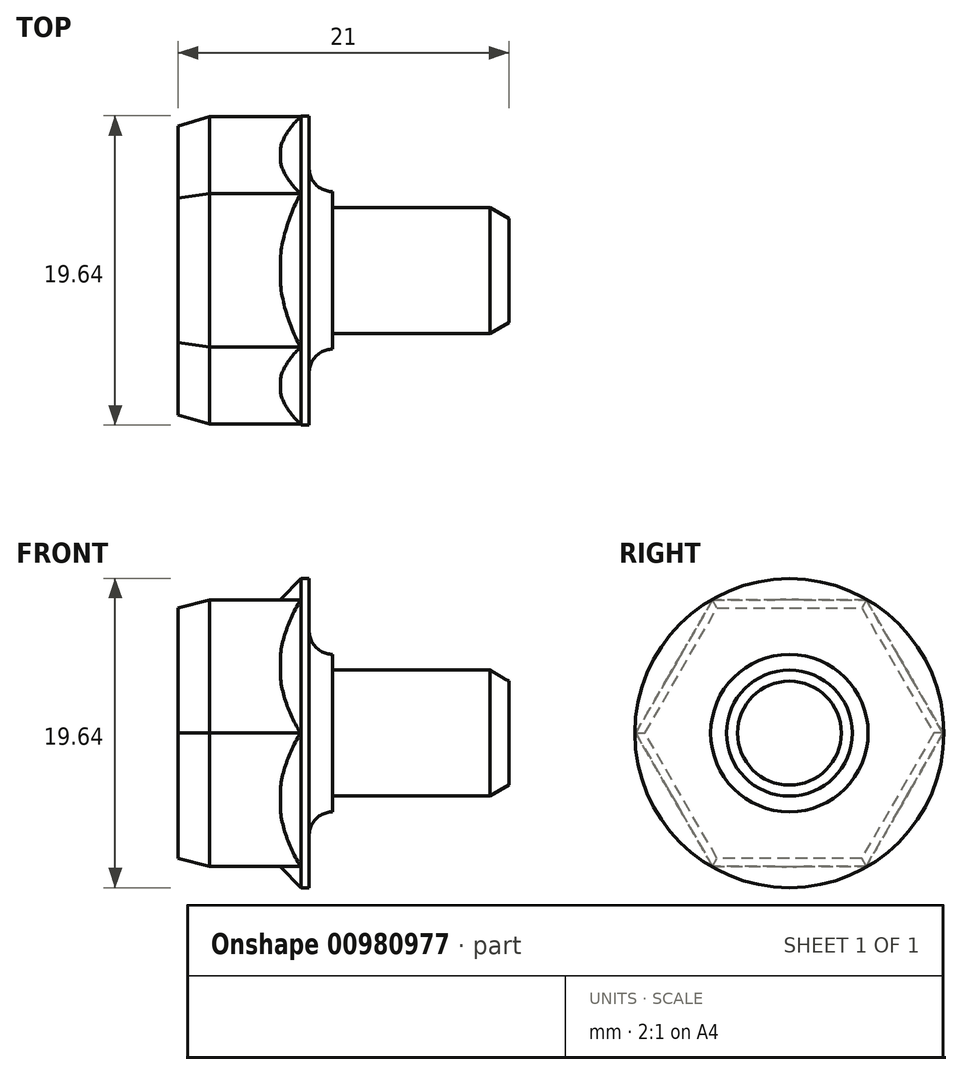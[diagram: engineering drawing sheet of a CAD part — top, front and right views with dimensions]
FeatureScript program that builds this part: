
annotation { "Feature Type Name" : "Feature", "Feature Type Description" : "" }
export const myFeature = defineFeature(function(context is Context, id is Id, definition is map)
    precondition{}
    {
        {
            var Q0;
            Q0=qCreatedBy(makeId("Right.planeOp"),FACE);
            var sketch = newSketch(context, id + "F0", { "sketchPlane" : qUnion([Q0])});
            skCircle(sketch, "E0.cCircle", {"center": v(0, 0) * mm, "radius": 8.45 * mm, "construction": true});
            skLineSegment(sketch, "E0.0", {"start": v(-4.88, 8.45) * mm, "end": v(4.88, 8.45) * mm});
            skLineSegment(sketch, "E0.1", {"start": v(4.88, 8.45) * mm, "end": v(9.76, 0) * mm});
            skLineSegment(sketch, "E0.2", {"start": v(9.76, 0) * mm, "end": v(4.88, -8.45) * mm});
            skLineSegment(sketch, "E0.3", {"start": v(4.88, -8.45) * mm, "end": v(-4.88, -8.45) * mm});
            skLineSegment(sketch, "E0.4", {"start": v(-4.88, -8.45) * mm, "end": v(-9.76, 0) * mm});
            skLineSegment(sketch, "E0.5", {"start": v(-9.76, 0) * mm, "end": v(-4.88, 8.45) * mm});
            skPoint(sketch, "E0.0.midPoint", {"position": v(0, 8.45) * mm});
            skSolve(sketch);
        }
        {
            var Q0;
            Q0=makeQuery(id+"F0.imprint","IMPRINT",FACE,{"disambiguationData":[TD([[makeQuery(id+"F0.imprint","IMPRINT",EDGE,{"derivedFrom":sQuery(id+"F0.wireOp",EDGE,"E0.0")}),-1.0]])]});
            extrude(context, id + "F1", {"entities" : qUnion([Q0]), "depth" : 8 * mm, "offsetDistance" : 25 * mm});
        }
        {
            var Q0;
            Q0=qCreatedBy(makeId("Front.planeOp"),FACE);
            var sketch = newSketch(context, id + "F2", { "sketchPlane" : qUnion([Q0])});
            skLineSegment(sketch, "E1", {"start": v(-6.63, 0) * mm, "end": v(40.7, 0) * mm, "construction": true});
            skLineSegment(sketch, "E2.bottom", {"start": v(6.5, 0) * mm, "end": v(8.31, 0) * mm});
            skLineSegment(sketch, "E2.top", {"start": v(6.5, 9.81) * mm, "end": v(8.31, 9.81) * mm});
            skLineSegment(sketch, "E2.left", {"start": v(6.5, 0) * mm, "end": v(6.5, 9.81) * mm});
            skLineSegment(sketch, "E2.right", {"start": v(8.32, 0) * mm, "end": v(8.31, 9.81) * mm});
            skLineSegment(sketch, "E3.top", {"start": v(9.81, 4) * mm, "end": v(21, 4) * mm});
            skLineSegment(sketch, "E3.right", {"start": v(21, 0) * mm, "end": v(21, 4) * mm});
            skLineSegment(sketch, "E4", {"start": v(7.81, 9.81) * mm, "end": v(6.5, 8.5) * mm});
            skArc(sketch, "E5", {"start": v(8.31, 6.5) * mm, "mid": v(8.75, 5.44) * mm, "end": v(9.81, 5) * mm});
            skLineSegment(sketch, "E6", {"start": v(9.81, 5) * mm, "end": v(18.14, 5) * mm, "construction": true});
            skLineSegment(sketch, "E7", {"start": v(9.81, 5) * mm, "end": v(9.81, 4) * mm});
            skLineSegment(sketch, "E8", {"start": v(8.31, 0) * mm, "end": v(21, 0) * mm});
            skSolve(sketch);
        }
        {
            var Q0;
            Q0=makeQuery(id+"F2.imprint","IMPRINT",FACE,{"disambiguationData":[TD([[makeQuery(id+"F2.imprint","IMPRINT",EDGE,{"derivedFrom":sQuery(id+"F2.wireOp",EDGE,"E2.right")}),-1.0]])]});
            var Q1;
            Q1=makeQuery(id+"F2.imprint","IMPRINT",FACE,{"disambiguationData":[TD([[makeQuery(id+"F2.imprint","IMPRINT",EDGE,{"derivedFrom":sQuery(id+"F2.wireOp",EDGE,"E3.bottom")}),1.0]])]});
            var Q2;
            Q2=makeQuery(id+"F2.imprint","IMPRINT",FACE,{"disambiguationData":[TD([[makeQuery(id+"F2.imprint","IMPRINT",EDGE,{"derivedFrom":sQuery(id+"F2.wireOp",EDGE,"E2.bottom")}),1.0]])]});
            var Q3;
            Q3=sQuery(id+"F2.wireOp",EDGE,"E1");
            revolve(context, id + "F3", {"operationType" : NewBodyOperationType.ADD, "surfaceOperationType" : NewSurfaceOperationType.NEW, "entities" : qUnion([Q0, Q1, Q2]), "axis" : qUnion([Q3]), "revolveType" : RevolveType.FULL});
        }
        {
            var Q0;
            Q0=makeQuery(id+"F1.opExtrude","CAP_FACE",FACE,{"disambiguationData":[OSD([sQuery(id+"F0.wireOp",EDGE,"E0.0"),sQuery(id+"F0.wireOp",EDGE,"E0.1"),sQuery(id+"F0.wireOp",EDGE,"E0.2"),sQuery(id+"F0.wireOp",EDGE,"E0.3"),sQuery(id+"F0.wireOp",EDGE,"E0.4"),sQuery(id+"F0.wireOp",EDGE,"E0.5")])],"isStart":true});
            chamfer(context, id + "F4", {"entities" : qUnion([Q0]), "chamferType" : ChamferType.TWO_OFFSETS, "width1" : 0.5 * mm, "oppositeDirection" : false, "width2" : 2 * mm, "tangentPropagation" : true});
        }
        {
            var Q0;
            Q0=makeQuery(id+"F3.opRevolve","SWEPT_EDGE",EDGE,{"disambiguationData":[OSD([sQuery(id+"F2.wireOp",EDGE,"E3.top"),sQuery(id+"F2.wireOp",EDGE,"E3.right")])]});
            chamfer(context, id + "F5", {"entities" : qUnion([Q0]), "chamferType" : ChamferType.TWO_OFFSETS, "width1" : 1.2 * mm, "oppositeDirection" : false, "width2" : 0.7 * mm, "tangentPropagation" : true});
        }
    });
